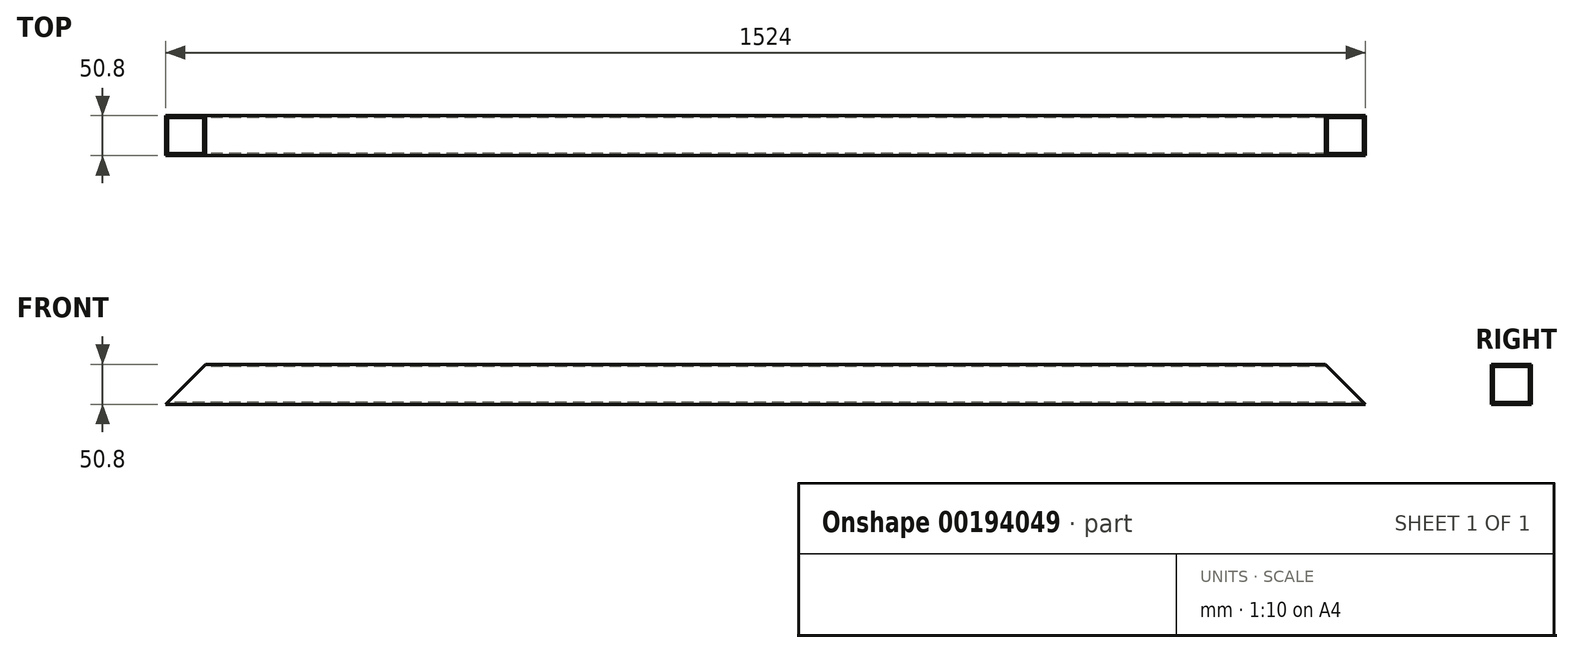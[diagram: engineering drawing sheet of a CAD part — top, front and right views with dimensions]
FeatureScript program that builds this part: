
annotation { "Feature Type Name" : "Feature", "Feature Type Description" : "" }
export const myFeature = defineFeature(function(context is Context, id is Id, definition is map)
    precondition{}
    {
        {
            var Q0;
            Q0=qCreatedBy(makeId("Top.planeOp"),FACE);
            var sketch = newSketch(context, id + "F0", { "sketchPlane" : qUnion([Q0])});
            skLineSegment(sketch, "E0.bottom", {"start": v(762, -25.4) * mm, "end": v(-762, -25.4) * mm});
            skLineSegment(sketch, "E0.top", {"start": v(762, 25.4) * mm, "end": v(-762, 25.4) * mm});
            skLineSegment(sketch, "E0.left", {"start": v(762, -25.4) * mm, "end": v(762, 25.4) * mm});
            skLineSegment(sketch, "E0.right", {"start": v(-762, -25.4) * mm, "end": v(-762, 25.4) * mm});
            skPoint(sketch, "E0.middle", {"position": v(0, 0) * mm});
            skSolve(sketch);
        }
        {
            var Q0;
            Q0=makeQuery(id+"F0.imprint","IMPRINT",FACE,{"disambiguationData":[TD([[makeQuery(id+"F0.imprint","IMPRINT",EDGE,{"derivedFrom":sQuery(id+"F0.wireOp",EDGE,"E0.bottom")}),-1.0]])]});
            extrude(context, id + "F1", {"entities" : qUnion([Q0]), "depth" : 50.8 * mm});
        }
        {
            var Q0;
            Q0=makeQuery(id+"F1.opExtrude","SWEPT_FACE",FACE,{"disambiguationData":[OSD([sQuery(id+"F0.wireOp",EDGE,"E0.right")])]});
            var Q1;
            Q1=makeQuery(id+"F1.opExtrude","SWEPT_FACE",FACE,{"disambiguationData":[OSD([sQuery(id+"F0.wireOp",EDGE,"E0.left")])]});
            shell(context, id + "F2", {"entities" : qUnion([Q0, Q1]), "thickness" : 2.54 * mm});
        }
        {
            var Q0;
            Q0=makeQuery(id+"F1.opExtrude","SWEPT_FACE",FACE,{"disambiguationData":[OSD([sQuery(id+"F0.wireOp",EDGE,"E0.bottom")])]});
            var sketch = newSketch(context, id + "F3", { "sketchPlane" : qUnion([Q0])});
            skLineSegment(sketch, "E1", {"start": v(762, 0) * mm, "end": v(711.2, 50.8) * mm});
            skLineSegment(sketch, "E2", {"start": v(711.2, 50.8) * mm, "end": v(762, 50.8) * mm});
            skLineSegment(sketch, "E3", {"start": v(762, 50.8) * mm, "end": v(762, 0) * mm});
            skSolve(sketch);
        }
        {
            var Q0;
            Q0 = qSketchRegion(id + "F3", true);
            extrude(context, id + "F4", {"entities" : qUnion([Q0]), "operationType" : NewBodyOperationType.REMOVE, "endBound" : BoundingType.THROUGH_ALL, "oppositeDirection" : true, "depth" : 25.4 * mm});
        }
        {
            var Q0;
            Q0=makeQuery(id+"F1.opExtrude","SWEPT_FACE",FACE,{"disambiguationData":[OSD([sQuery(id+"F0.wireOp",EDGE,"E0.bottom")])]});
            var sketch = newSketch(context, id + "F5", { "sketchPlane" : qUnion([Q0])});
            skLineSegment(sketch, "E4", {"start": v(-762, 0) * mm, "end": v(-762, 50.8) * mm});
            skLineSegment(sketch, "E5", {"start": v(-762, 50.8) * mm, "end": v(-711.2, 50.8) * mm});
            skLineSegment(sketch, "E6", {"start": v(-711.2, 50.8) * mm, "end": v(-762, 0) * mm});
            skSolve(sketch);
        }
        {
            var Q0;
            Q0=makeQuery(id+"F5.imprint","IMPRINT",FACE,{"disambiguationData":[TD([[makeQuery(id+"F5.imprint","IMPRINT",EDGE,{"derivedFrom":sQuery(id+"F5.wireOp",EDGE,"E4")}),1.0]])]});
            extrude(context, id + "F6", {"entities" : qUnion([Q0]), "operationType" : NewBodyOperationType.REMOVE, "endBound" : BoundingType.THROUGH_ALL, "oppositeDirection" : true, "depth" : 25.4 * mm});
        }
    });
